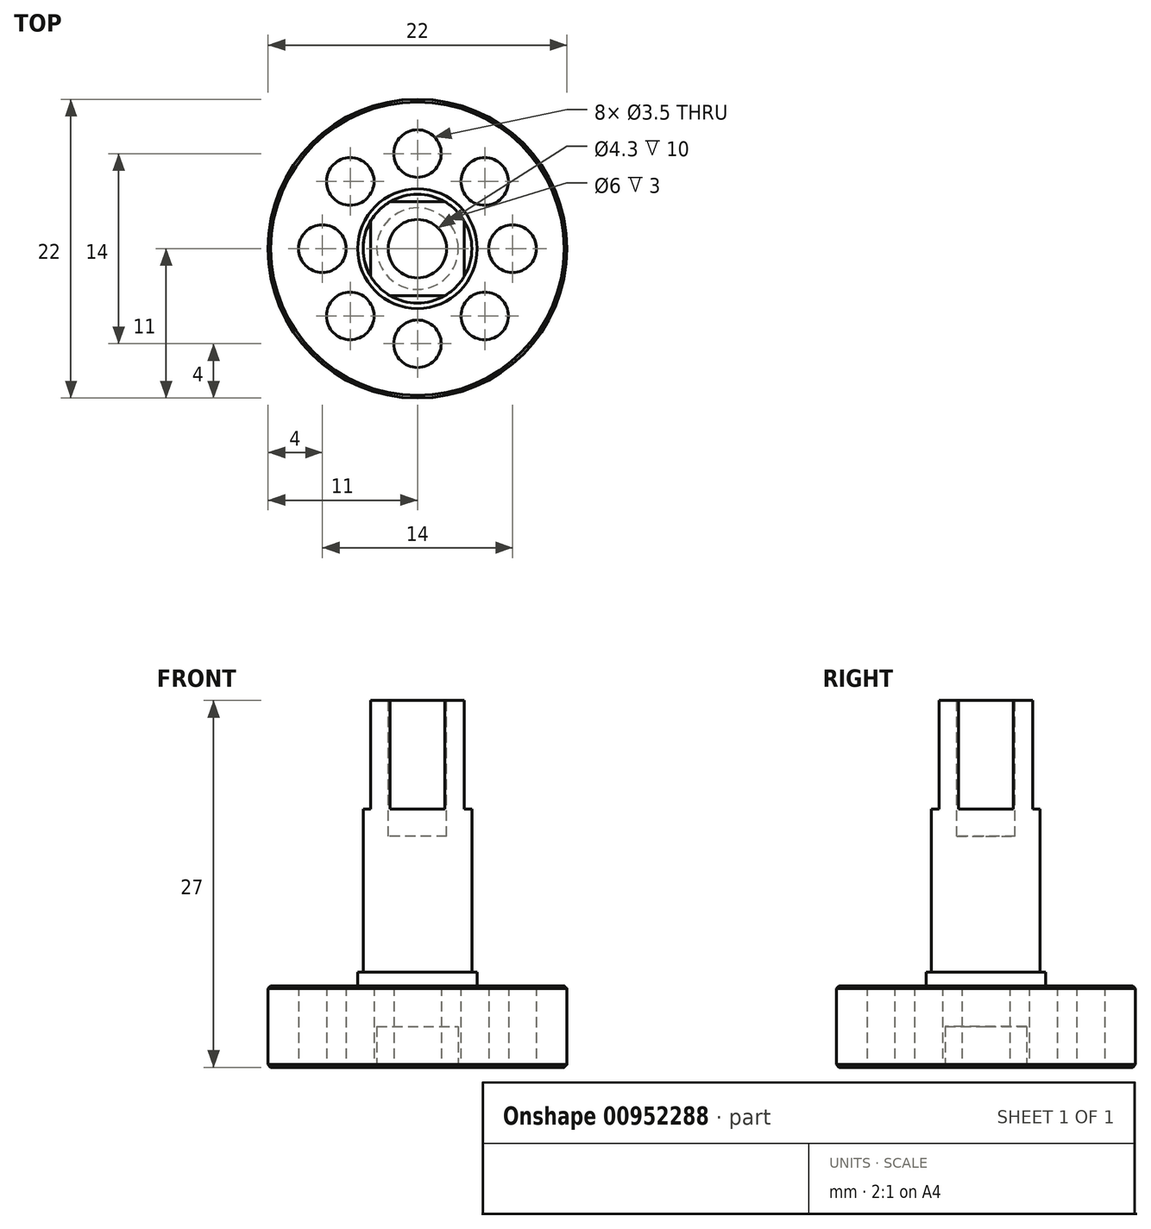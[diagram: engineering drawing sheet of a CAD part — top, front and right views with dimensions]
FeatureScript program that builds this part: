
annotation { "Feature Type Name" : "Feature", "Feature Type Description" : "" }
export const myFeature = defineFeature(function(context is Context, id is Id, definition is map)
    precondition{}
    {
        {
            var Q0;
            Q0=qCreatedBy(makeId("Top.planeOp"),FACE);
            var sketch = newSketch(context, id + "F0", { "sketchPlane" : qUnion([Q0])});
            skCircle(sketch, "E0", {"center": v(0, 0) * mm, "radius": 11 * mm});
            skSolve(sketch);
        }
        {
            var Q0;
            Q0=qSketchRegion(id+"F0",true);
            extrude(context, id + "F1", {"entities" : qUnion([Q0]), "depth" : 6 * mm, "offsetDistance" : 25 * mm});
        }
        {
            var Q0;
            Q0=makeQuery(id+"F1.opExtrude","CAP_FACE",FACE,{"disambiguationData":[OSD([sQuery(id+"F0.wireOp",EDGE,"E0")])],"isStart":false});
            var sketch = newSketch(context, id + "F2", { "sketchPlane" : qUnion([Q0])});
            skCircle(sketch, "E1", {"center": v(0, 0) * mm, "radius": 4 * mm});
            skSolve(sketch);
        }
        {
            var Q0;
            Q0=qSketchRegion(id+"F2",true);
            extrude(context, id + "F3", {"entities" : qUnion([Q0]), "operationType" : NewBodyOperationType.ADD, "depth" : 21 * mm, "offsetDistance" : 25 * mm});
        }
        {
            var Q0;
            Q0=makeQuery(id+"F1.opExtrude","CAP_FACE",FACE,{"disambiguationData":[OSD([sQuery(id+"F0.wireOp",EDGE,"E0")])],"isStart":false});
            var sketch = newSketch(context, id + "F4", { "sketchPlane" : qUnion([Q0])});
            skCircle(sketch, "E2", {"center": v(0, 0) * mm, "radius": 4.4 * mm});
            skSolve(sketch);
        }
        {
            var Q0;
            Q0=qSketchRegion(id+"F4",true);
            extrude(context, id + "F5", {"entities" : qUnion([Q0]), "operationType" : NewBodyOperationType.ADD, "depth" : 1 * mm, "offsetDistance" : 25 * mm});
        }
        {
            var Q0;
            Q0=makeQuery(id+"F3.opExtrude","CAP_FACE",FACE,{"disambiguationData":[OSD([sQuery(id+"F2.wireOp",EDGE,"E1")])],"isStart":false});
            var sketch = newSketch(context, id + "F6", { "sketchPlane" : qUnion([Q0])});
            skLineSegment(sketch, "E3.bottom", {"start": v(3.45, -3.45) * mm, "end": v(-3.45, -3.45) * mm});
            skLineSegment(sketch, "E3.top", {"start": v(3.45, 3.45) * mm, "end": v(-3.45, 3.45) * mm});
            skLineSegment(sketch, "E3.left", {"start": v(3.45, -3.45) * mm, "end": v(3.45, 3.45) * mm});
            skLineSegment(sketch, "E3.right", {"start": v(-3.45, -3.45) * mm, "end": v(-3.45, 3.45) * mm});
            skPoint(sketch, "E3.middle", {"position": v(0, 0) * mm});
            skLineSegment(sketch, "E4.bottom", {"start": v(5, -5) * mm, "end": v(-5, -5) * mm});
            skLineSegment(sketch, "E4.top", {"start": v(5, 5) * mm, "end": v(-5, 5) * mm});
            skLineSegment(sketch, "E4.left", {"start": v(5, -5) * mm, "end": v(5, 5) * mm});
            skLineSegment(sketch, "E4.right", {"start": v(-5, -5) * mm, "end": v(-5, 5) * mm});
            skSolve(sketch);
        }
        {
            var Q0;
            Q0=qSketchRegion(id+"F6",true);
            extrude(context, id + "F7", {"entities" : qUnion([Q0]), "operationType" : NewBodyOperationType.REMOVE, "oppositeDirection" : true, "depth" : 8 * mm, "offsetDistance" : 25 * mm});
        }
        {
            var Q0;
            Q0=makeQuery(id+"F1.opExtrude","CAP_FACE",FACE,{"disambiguationData":[OSD([sQuery(id+"F0.wireOp",EDGE,"E0")])],"isStart":true});
            var sketch = newSketch(context, id + "F8", { "sketchPlane" : qUnion([Q0])});
            skCircle(sketch, "E5", {"center": v(0, 7) * mm, "radius": 1.75 * mm});
            skCircle(sketch, "E6.1.0", {"center": v(-4.95, 4.95) * mm, "radius": 1.75 * mm});
            skCircle(sketch, "E6.2.0", {"center": v(-7, 0) * mm, "radius": 1.75 * mm});
            skCircle(sketch, "E6.3.0", {"center": v(-4.95, -4.95) * mm, "radius": 1.75 * mm});
            skCircle(sketch, "E6.4.0", {"center": v(0, -7) * mm, "radius": 1.75 * mm});
            skCircle(sketch, "E6.5.0", {"center": v(4.95, -4.95) * mm, "radius": 1.75 * mm});
            skCircle(sketch, "E6.6.0", {"center": v(7, 0) * mm, "radius": 1.75 * mm});
            skCircle(sketch, "E6.7.0", {"center": v(4.95, 4.95) * mm, "radius": 1.75 * mm});
            skPoint(sketch, "E6.center", {"position": v(0, 0) * mm});
            skSolve(sketch);
        }
        {
            var Q0;
            Q0=qSketchRegion(id+"F8",true);
            extrude(context, id + "F9", {"entities" : qUnion([Q0]), "operationType" : NewBodyOperationType.REMOVE, "oppositeDirection" : true, "depth" : 25 * mm, "offsetDistance" : 25 * mm});
        }
        {
            var Q0;
            Q0=makeQuery(id+"F1.opExtrude","CAP_FACE",FACE,{"disambiguationData":[OSD([sQuery(id+"F0.wireOp",EDGE,"E0")])],"isStart":true});
            var sketch = newSketch(context, id + "F10", { "sketchPlane" : qUnion([Q0])});
            skCircle(sketch, "E7", {"center": v(0, 0) * mm, "radius": 3 * mm});
            skSolve(sketch);
        }
        {
            var Q0;
            Q0=makeQuery(id+"F1.opExtrude","SWEPT_FACE",FACE,{"disambiguationData":[OSD([sQuery(id+"F0.wireOp",EDGE,"E0")])]});
            chamfer(context, id + "F11", {"entities" : qUnion([Q0]), "width" : 0.2 * mm, "tangentPropagation" : true});
        }
        {
            var Q0;
            Q0=makeQuery(id+"F3.opExtrude","CAP_FACE",FACE,{"disambiguationData":[OSD([sQuery(id+"F2.wireOp",EDGE,"E1")])],"isStart":false});
            var sketch = newSketch(context, id + "F12", { "sketchPlane" : qUnion([Q0])});
            skCircle(sketch, "E8", {"center": v(0, 0) * mm, "radius": 2.15 * mm});
            skSolve(sketch);
        }
        {
            var Q0;
            Q0=qSketchRegion(id+"F12",true);
            extrude(context, id + "F13", {"entities" : qUnion([Q0]), "operationType" : NewBodyOperationType.REMOVE, "oppositeDirection" : true, "depth" : 10 * mm, "offsetDistance" : 25 * mm});
        }
        {
            var Q0;
            Q0=makeQuery(id+"F10.imprint","IMPRINT",FACE,{"disambiguationData":[TD([[makeQuery(id+"F10.imprint","IMPRINT",EDGE,{"derivedFrom":sQuery(id+"F10.wireOp",EDGE,"E7")}),1.0]])]});
            extrude(context, id + "F14", {"entities" : qUnion([Q0]), "operationType" : NewBodyOperationType.REMOVE, "oppositeDirection" : true, "depth" : 3 * mm, "offsetDistance" : 25 * mm});
        }
    });
